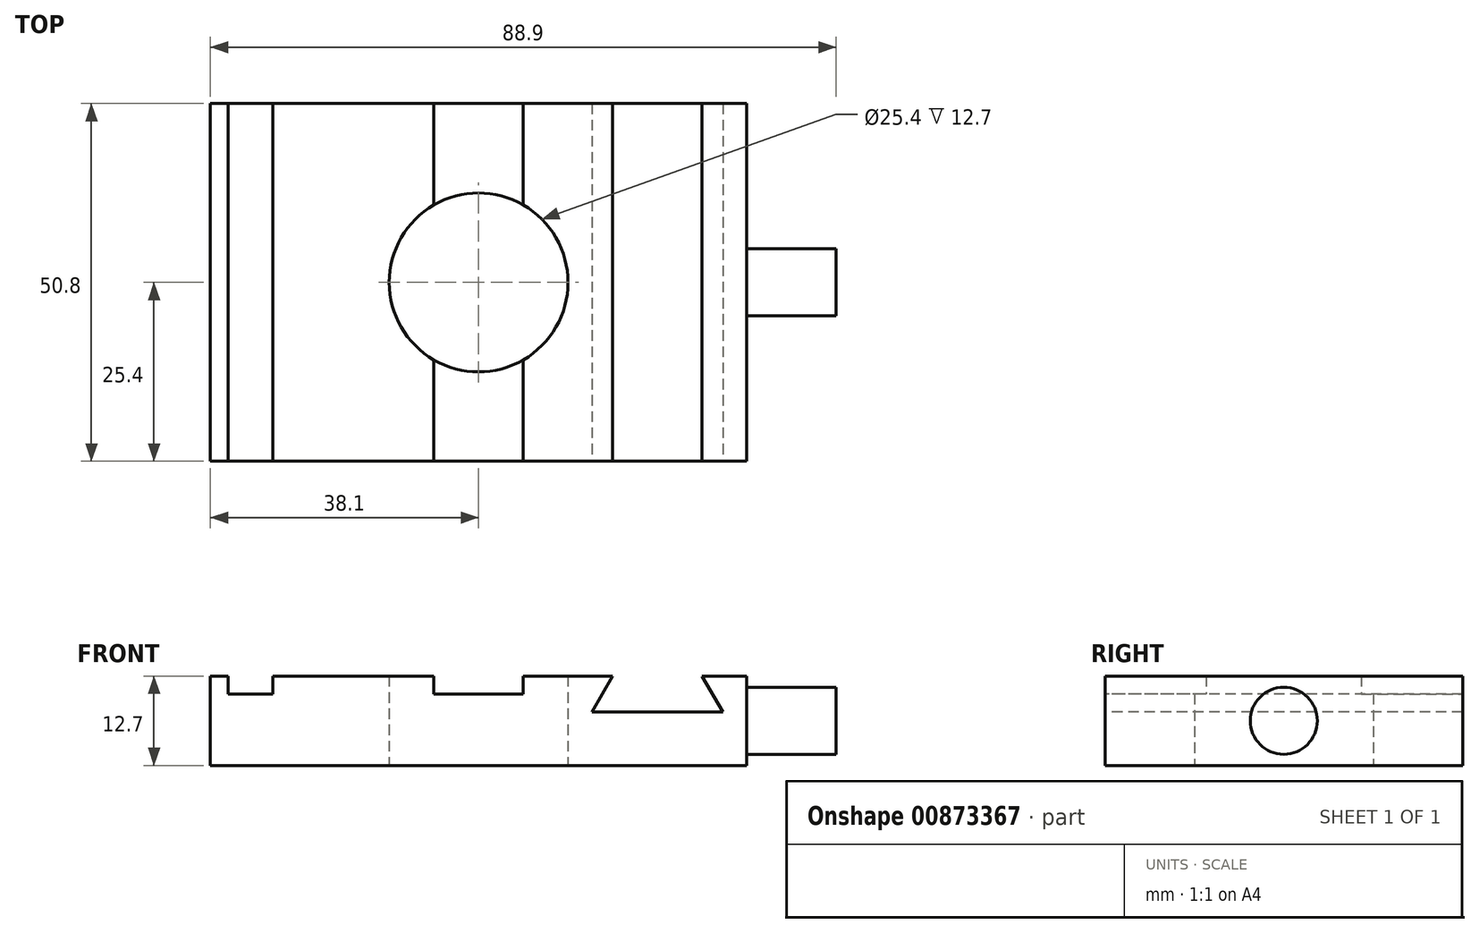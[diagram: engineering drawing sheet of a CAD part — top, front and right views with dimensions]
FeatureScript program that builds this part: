
annotation { "Feature Type Name" : "Feature", "Feature Type Description" : "" }
export const myFeature = defineFeature(function(context is Context, id is Id, definition is map)
    precondition{}
    {
        {
            var Q0;
            Q0=qCreatedBy(makeId("Top.planeOp"),FACE);
            var sketch = newSketch(context, id + "F0", { "sketchPlane" : qUnion([Q0])});
            skLineSegment(sketch, "E0.bottom", {"start": v(38.1, -25.4) * mm, "end": v(-38.1, -25.4) * mm});
            skLineSegment(sketch, "E0.top", {"start": v(38.1, 25.4) * mm, "end": v(-38.1, 25.4) * mm});
            skLineSegment(sketch, "E0.left", {"start": v(38.1, -25.4) * mm, "end": v(38.1, 25.4) * mm});
            skLineSegment(sketch, "E0.right", {"start": v(-38.1, -25.4) * mm, "end": v(-38.1, 25.4) * mm});
            skPoint(sketch, "E0.middle", {"position": v(0, 0) * mm});
            skCircle(sketch, "E1", {"center": v(0, 0) * mm, "radius": 12.7 * mm});
            skSolve(sketch);
        }
        {
            var Q0;
            Q0=makeQuery(id+"F0.imprint","IMPRINT",FACE,{"disambiguationData":[TD([[makeQuery(id+"F0.imprint","IMPRINT",EDGE,{"derivedFrom":sQuery(id+"F0.wireOp",EDGE,"E0.bottom")}),-1.0]])]});
            extrude(context, id + "F1", {"entities" : qUnion([Q0]), "depth" : 12.7 * mm, "offsetDistance" : 25.4 * mm});
        }
        {
            var Q0;
            Q0=makeQuery(id+"F1.opExtrude","CAP_FACE",FACE,{"disambiguationData":[OSD([sQuery(id+"F0.wireOp",EDGE,"E0.bottom"),sQuery(id+"F0.wireOp",EDGE,"E0.top"),sQuery(id+"F0.wireOp",EDGE,"E0.left"),sQuery(id+"F0.wireOp",EDGE,"E0.right"),sQuery(id+"F0.wireOp",EDGE,"E1")])],"isStart":false});
            var sketch = newSketch(context, id + "F2", { "sketchPlane" : qUnion([Q0])});
            skLineSegment(sketch, "E2.bottom", {"start": v(-35.56, 25.4) * mm, "end": v(-29.21, 25.4) * mm});
            skLineSegment(sketch, "E2.top", {"start": v(-35.56, -25.4) * mm, "end": v(-29.21, -25.4) * mm});
            skLineSegment(sketch, "E2.left", {"start": v(-35.56, 25.4) * mm, "end": v(-35.56, -25.4) * mm});
            skLineSegment(sketch, "E2.right", {"start": v(-29.21, 25.4) * mm, "end": v(-29.21, -25.4) * mm});
            skLineSegment(sketch, "E3", {"start": v(-6.35, 25.4) * mm, "end": v(-6.35, -25.4) * mm});
            skLineSegment(sketch, "E4", {"start": v(-6.35, -25.4) * mm, "end": v(6.35, -25.4) * mm});
            skLineSegment(sketch, "E5", {"start": v(6.35, -25.4) * mm, "end": v(6.35, 25.4) * mm});
            skLineSegment(sketch, "E6", {"start": v(6.35, 25.4) * mm, "end": v(-6.35, 25.4) * mm});
            skLineSegment(sketch, "E7", {"start": v(0, 25.4) * mm, "end": v(0, -25.4) * mm, "construction": true});
            skSolve(sketch);
        }
        {
            var Q0;
            Q0 = qSketchRegion(id + "F2", true);
            extrude(context, id + "F3", {"entities" : qUnion([Q0]), "operationType" : NewBodyOperationType.REMOVE, "oppositeDirection" : true, "depth" : 2.54 * mm, "offsetDistance" : 25.4 * mm});
        }
        {
            var Q0;
            Q0=makeQuery(id+"F1.opExtrude","SWEPT_FACE",FACE,{"disambiguationData":[OSD([sQuery(id+"F0.wireOp",EDGE,"E0.bottom")])]});
            var sketch = newSketch(context, id + "F4", { "sketchPlane" : qUnion([Q0])});
            skLineSegment(sketch, "E8", {"start": v(19.05, 12.7) * mm, "end": v(31.75, 12.7) * mm});
            skLineSegment(sketch, "E9", {"start": v(31.75, 12.7) * mm, "end": v(34.68, 7.62) * mm});
            skLineSegment(sketch, "E10", {"start": v(34.68, 7.62) * mm, "end": v(16.12, 7.62) * mm});
            skLineSegment(sketch, "E11", {"start": v(16.12, 7.62) * mm, "end": v(19.05, 12.7) * mm});
            skLineSegment(sketch, "E12", {"start": v(25.4, 7.62) * mm, "end": v(25.4, 12.7) * mm, "construction": true});
            skSolve(sketch);
        }
        {
            var Q0;
            Q0=makeQuery(id+"F4.imprint","IMPRINT",FACE,{"disambiguationData":[TD([[makeQuery(id+"F4.imprint","IMPRINT",EDGE,{"derivedFrom":sQuery(id+"F4.wireOp",EDGE,"E8")}),1.0]])]});
            extrude(context, id + "F5", {"entities" : qUnion([Q0]), "operationType" : NewBodyOperationType.REMOVE, "endBound" : BoundingType.THROUGH_ALL, "oppositeDirection" : true, "depth" : 25.4 * mm, "offsetDistance" : 25.4 * mm});
        }
        {
            var Q0;
            Q0=makeQuery(id+"F1.opExtrude","SWEPT_FACE",FACE,{"disambiguationData":[OSD([sQuery(id+"F0.wireOp",EDGE,"E0.left")])]});
            var sketch = newSketch(context, id + "F6", { "sketchPlane" : qUnion([Q0])});
            skCircle(sketch, "E13", {"center": v(0, 6.35) * mm, "radius": 4.76 * mm});
            skPoint(sketch, "E13.centerSnap0", {"position": v(-25.4, 6.35) * mm});
            skPoint(sketch, "E13.centerSnap1", {"position": v(0, 12.7) * mm});
            skSolve(sketch);
        }
        {
            var Q0;
            Q0=makeQuery(id+"F6.imprint","IMPRINT",FACE,{"disambiguationData":[TD([[makeQuery(id+"F6.imprint","IMPRINT",EDGE,{"derivedFrom":sQuery(id+"F6.wireOp",EDGE,"E13")}),1.0]])]});
            extrude(context, id + "F7", {"entities" : qUnion([Q0]), "operationType" : NewBodyOperationType.ADD, "depth" : 12.7 * mm, "offsetDistance" : 25.4 * mm});
        }
    });
